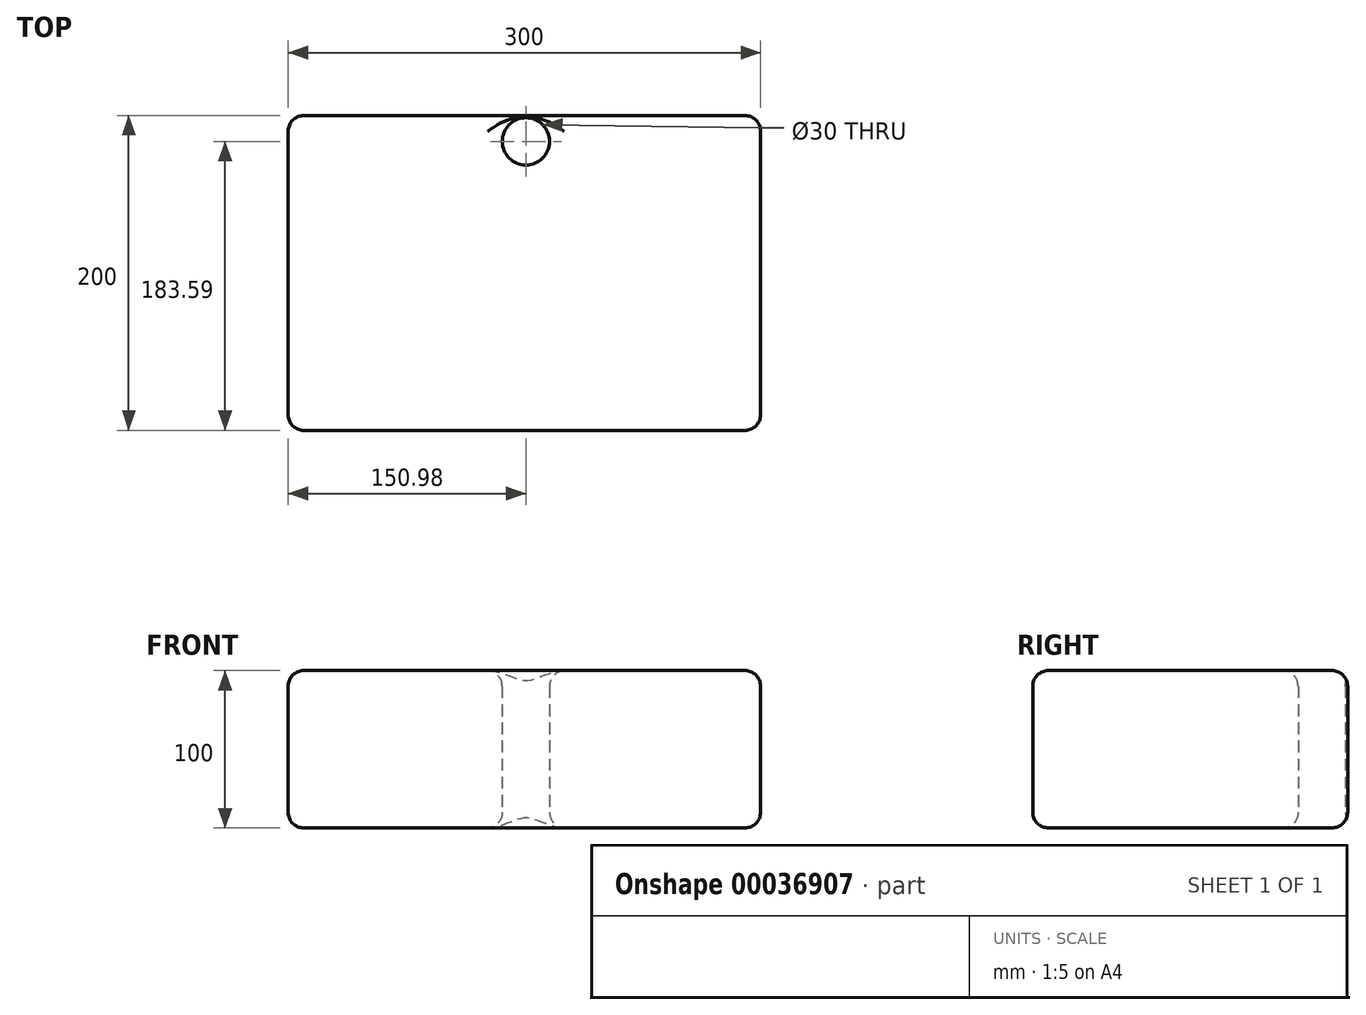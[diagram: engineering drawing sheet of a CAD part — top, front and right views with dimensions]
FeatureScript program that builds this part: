
annotation { "Feature Type Name" : "Feature", "Feature Type Description" : "" }
export const myFeature = defineFeature(function(context is Context, id is Id, definition is map)
    precondition{}
    {
        {
            var Q0;
            Q0=qCreatedBy(makeId("Top.planeOp"),FACE);
            var sketch = newSketch(context, id + "F0", { "sketchPlane" : qUnion([Q0])});
            skLineSegment(sketch, "E0.bottom", {"start": v(-150.98, 116.53) * mm, "end": v(149.02, 116.53) * mm});
            skLineSegment(sketch, "E0.top", {"start": v(-150.98, -83.47) * mm, "end": v(149.02, -83.47) * mm});
            skLineSegment(sketch, "E0.left", {"start": v(-150.98, 116.53) * mm, "end": v(-150.98, -83.47) * mm});
            skLineSegment(sketch, "E0.right", {"start": v(149.02, 116.53) * mm, "end": v(149.02, -83.47) * mm});
            skCircle(sketch, "E1", {"center": v(0, 100.12) * mm, "radius": 15 * mm});
            skSolve(sketch);
        }
        {
            var Q0;
            Q0=makeQuery(id+"F0.imprint","IMPRINT",FACE,{"disambiguationData":[TD([[makeQuery(id+"F0.imprint","IMPRINT",EDGE,{"derivedFrom":sQuery(id+"F0.wireOp",EDGE,"E0.bottom")}),-1.0]])]});
            extrude(context, id + "F1", {"entities" : qUnion([Q0]), "depth" : 100 * mm});
        }
        {
            var Q0;
            Q0=makeQuery(id+"F1.opExtrude","SWEPT_EDGE",EDGE,{"disambiguationData":[OSD([sQuery(id+"F0.wireOp",EDGE,"E0.bottom"),sQuery(id+"F0.wireOp",EDGE,"E0.right")])]});
            fillet(context, id + "F2", {"entities" : qUnion([Q0]), "radius" : 10 * mm, "tangentPropagation" : true, "allowEdgeOverflow" : false});
        }
        {
            var Q0;
            Q0=makeQuery(id+"F1.opExtrude","SWEPT_EDGE",EDGE,{"disambiguationData":[OSD([sQuery(id+"F0.wireOp",EDGE,"E0.bottom"),sQuery(id+"F0.wireOp",EDGE,"E0.left")])]});
            fillet(context, id + "F3", {"entities" : qUnion([Q0]), "radius" : 10 * mm, "tangentPropagation" : true, "allowEdgeOverflow" : false});
        }
        {
            var Q0;
            Q0=makeQuery(id+"F1.opExtrude","SWEPT_EDGE",EDGE,{"disambiguationData":[OSD([sQuery(id+"F0.wireOp",EDGE,"E0.top"),sQuery(id+"F0.wireOp",EDGE,"E0.right")])]});
            fillet(context, id + "F4", {"entities" : qUnion([Q0]), "radius" : 10 * mm, "tangentPropagation" : true, "allowEdgeOverflow" : false});
        }
        {
            var Q0;
            Q0=makeQuery(id+"F1.opExtrude","SWEPT_EDGE",EDGE,{"disambiguationData":[OSD([sQuery(id+"F0.wireOp",EDGE,"E0.top"),sQuery(id+"F0.wireOp",EDGE,"E0.left")])]});
            fillet(context, id + "F5", {"entities" : qUnion([Q0]), "radius" : 10 * mm, "tangentPropagation" : true, "allowEdgeOverflow" : false});
        }
        {
            var Q0;
            Q0=makeQuery(id+"F1.opExtrude","CAP_FACE",FACE,{"disambiguationData":[OSD([sQuery(id+"F0.wireOp",EDGE,"E0.bottom"),sQuery(id+"F0.wireOp",EDGE,"E0.top"),sQuery(id+"F0.wireOp",EDGE,"E0.left"),sQuery(id+"F0.wireOp",EDGE,"E0.right"),sQuery(id+"F0.wireOp",EDGE,"E1")])],"isStart":false});
            fillet(context, id + "F6", {"entities" : qUnion([Q0]), "radius" : 10 * mm, "tangentPropagation" : true, "allowEdgeOverflow" : false});
        }
        {
            var Q0;
            Q0=makeQuery(id+"F1.opExtrude","CAP_FACE",FACE,{"disambiguationData":[OSD([sQuery(id+"F0.wireOp",EDGE,"E0.bottom"),sQuery(id+"F0.wireOp",EDGE,"E0.top"),sQuery(id+"F0.wireOp",EDGE,"E0.left"),sQuery(id+"F0.wireOp",EDGE,"E0.right"),sQuery(id+"F0.wireOp",EDGE,"E1")])],"isStart":true});
            fillet(context, id + "F7", {"entities" : qUnion([Q0]), "radius" : 10 * mm, "tangentPropagation" : true, "allowEdgeOverflow" : false});
        }
    });
